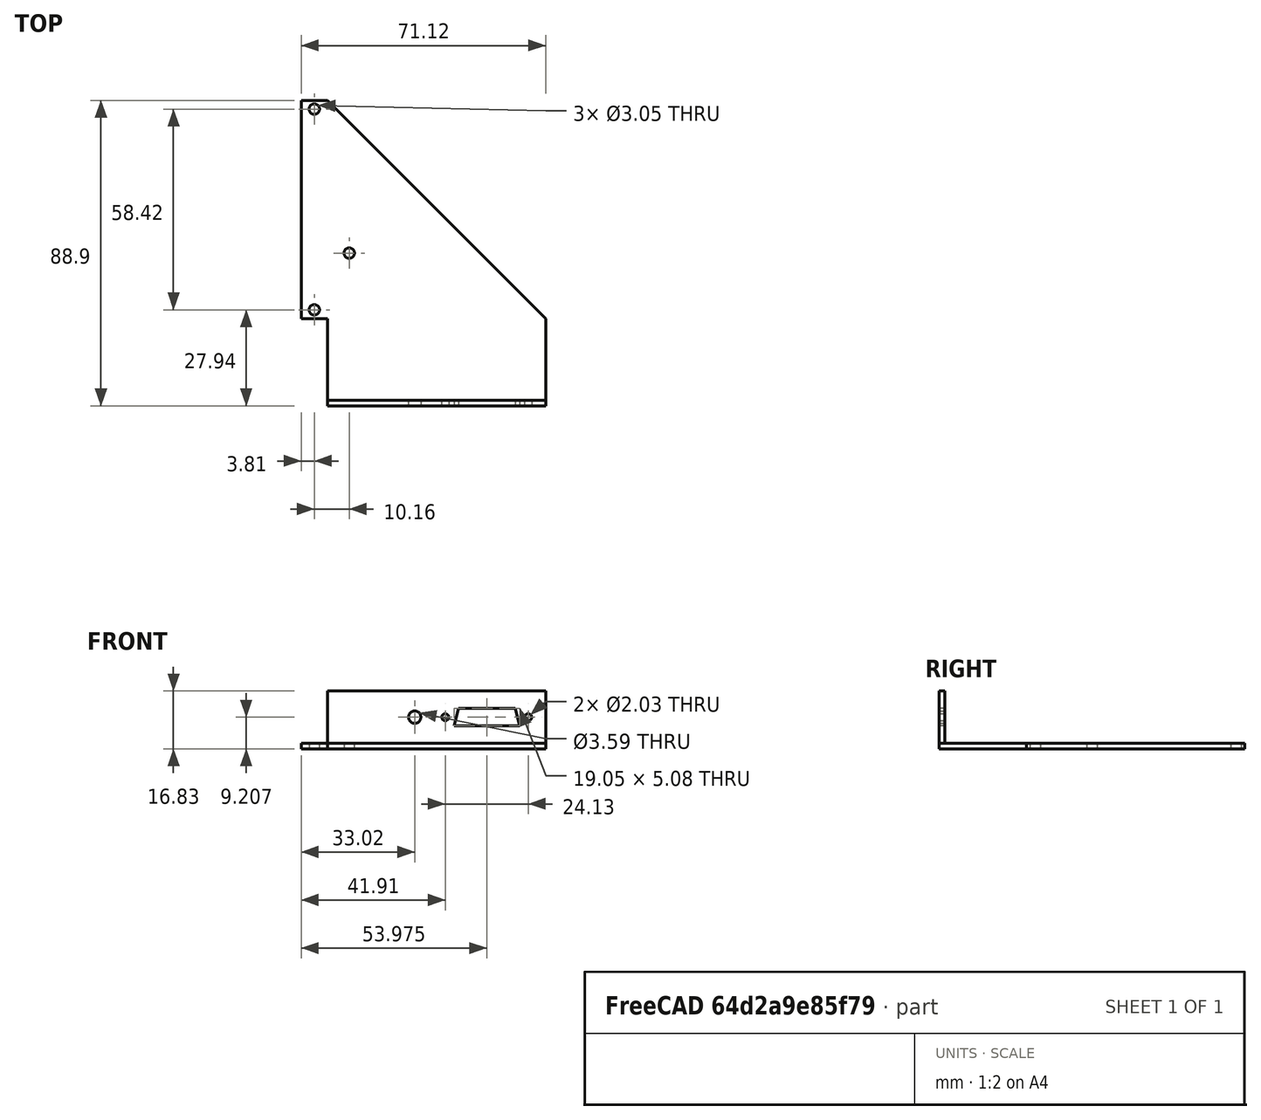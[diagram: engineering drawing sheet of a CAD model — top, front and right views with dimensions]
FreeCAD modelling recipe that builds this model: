
FCSTD DOCUMENT  (FreeCAD 0.19R24291 (Git))
Label: raspibrkt
License: All rights reserved
LicenseURL: http://en.wikipedia.org/wiki/All_rights_reserved
objects: Sketcher::SketchObject×2, PartDesign::Pad×2, PartDesign::Body×2
note: 8 computed .brp shape members not serialized (recipe doc carries the construction recipe); baked Part::Feature solids carry a one-line shape summary decoded from their .brp

FEATURE [Sketcher::SketchObject] Sketch
  FullyConstrained = false
  MapMode = 5
  Support = -> [XY_Plane]
  sketch-geometry (10):
    g0: LineSegment StartX=63.5 StartY=0 StartZ=0 EndX=-7.1e-15 EndY=63.5 EndZ=0
    g1: LineSegment StartX=-7.1e-15 StartY=63.5 StartZ=0 EndX=-7.62 EndY=63.5 EndZ=0
    g2: LineSegment StartX=-7.62 StartY=63.5 StartZ=0 EndX=-7.62 EndY=0 EndZ=0
    g3: LineSegment StartX=-7.62 StartY=0 StartZ=0 EndX=0 EndY=0 EndZ=0
    g4: LineSegment StartX=63.5 StartY=0 StartZ=0 EndX=63.5 EndY=-25.4 EndZ=0
    g5: LineSegment StartX=63.5 StartY=-25.4 StartZ=0 EndX=0 EndY=-25.4 EndZ=0
    g6: LineSegment StartX=0 StartY=-25.4 StartZ=0 EndX=0 EndY=0 EndZ=0
    g7: Circle CenterX=-3.81 CenterY=2.54 CenterZ=0 NormalX=0 NormalY=0 NormalZ=1 AngleXU=0 Radius=1.524
    g8: Circle CenterX=-3.81 CenterY=60.96 CenterZ=0 NormalX=0 NormalY=0 NormalZ=1 AngleXU=0 Radius=1.524
    g9: Circle CenterX=6.35 CenterY=19.05 CenterZ=0 NormalX=0 NormalY=0 NormalZ=1 AngleXU=0 Radius=1.524
  constraints (19):
    c: PointOnObject(g3,g-2)
    c: PointOnObject(g3,g-1)
    c: PointOnObject(g0,g-1)
    c: PointOnObject(g0,g-2)
    c: Coincident(g1,g0)
    c: Horizontal(g1)
    c: Coincident(g2,g1)
    c: PointOnObject(g2,g-1)
    c: Vertical(g2)
    c: Coincident(g3,g2)
    c: Coincident(g4,g0)
    c: Vertical(g4)
    c: Coincident(g5,g4)
    c: PointOnObject(g5,g-2)
    c: Horizontal(g5)
    c: Coincident(g6,g5)
    c: Radius(g7) = 1.524
    c: Radius(g8) = 1.524
    c: Radius(g9) = 1.524
FEATURE [PartDesign::Pad] Pad
  Direction = (1,1,1)
  Length = 1.5875
  Length2 = 99.9998
  Profile = -> Sketch
  Refine = true
  Type = 0
FEATURE [PartDesign::Body] Body  label="raspi_base"
  Group = -> [Sketch,Pad]
  Origin = -> Origin
  Tip = -> Pad
FEATURE [Sketcher::SketchObject] Sketch001
  FullyConstrained = false
  MapMode = 5
  Placement = pos=(0,0,0) rot=(1,0,0;1.5708rad)
  Support = -> [XZ_Plane001]
  sketch-geometry (11):
    g0: LineSegment StartX=0 StartY=0 StartZ=0 EndX=63.5 EndY=0 EndZ=0
    g1: LineSegment StartX=63.5 StartY=0 StartZ=0 EndX=63.5 EndY=15.24 EndZ=0
    g2: LineSegment StartX=63.5 StartY=15.24 StartZ=0 EndX=0 EndY=15.24 EndZ=0
    g3: LineSegment StartX=0 StartY=15.24 StartZ=0 EndX=0 EndY=0 EndZ=0
    g4: Circle CenterX=25.4 CenterY=7.62 CenterZ=0 NormalX=0 NormalY=0 NormalZ=1 AngleXU=0 Radius=1.79605
    g5: Circle CenterX=58.42 CenterY=7.62 CenterZ=0 NormalX=0 NormalY=0 NormalZ=1 AngleXU=0 Radius=1.016
    g6: Circle CenterX=34.29 CenterY=7.62 CenterZ=0 NormalX=0 NormalY=0 NormalZ=1 AngleXU=0 Radius=1.016
    g7: LineSegment StartX=38.1 StartY=10.16 StartZ=0 EndX=36.83 EndY=5.08 EndZ=0
    g8: LineSegment StartX=36.83 StartY=5.08 StartZ=0 EndX=55.88 EndY=5.08 EndZ=0
    g9: LineSegment StartX=55.88 StartY=5.08 StartZ=0 EndX=54.61 EndY=10.16 EndZ=0
    g10: LineSegment StartX=54.61 StartY=10.16 StartZ=0 EndX=38.1 EndY=10.16 EndZ=0
  constraints (17):
    c: Coincident(g0,g1)
    c: Coincident(g1,g2)
    c: Coincident(g2,g3)
    c: Coincident(g3,g0)
    c: Horizontal(g0)
    c: Horizontal(g2)
    c: Vertical(g1)
    c: Vertical(g3)
    c: Coincident(g0,g-1)
    c: Coincident(g8,g7)
    c: Horizontal(g8)
    c: Coincident(g9,g8)
    c: Coincident(g10,g9)
    c: Coincident(g10,g7)
    c: Horizontal(g10)
    c: Radius(g6) = 1.016
    c: Radius(g5) = 1.016
FEATURE [PartDesign::Pad] Pad001
  Direction = (1,1,1)
  Length = 1.5875
  Length2 = 99.9998
  Placement = pos=(0,0,0) rot=(1,0,0;1.5708rad)
  Profile = -> Sketch001
  Refine = true
  Type = 0
FEATURE [PartDesign::Body] Body001  label="raspi_cons"
  Group = -> [Sketch001,Pad001]
  Origin = -> Origin001
  Placement = pos=(0,-23.8125,1.5875) rot=(0,0,1;0rad)
  Tip = -> Pad001
